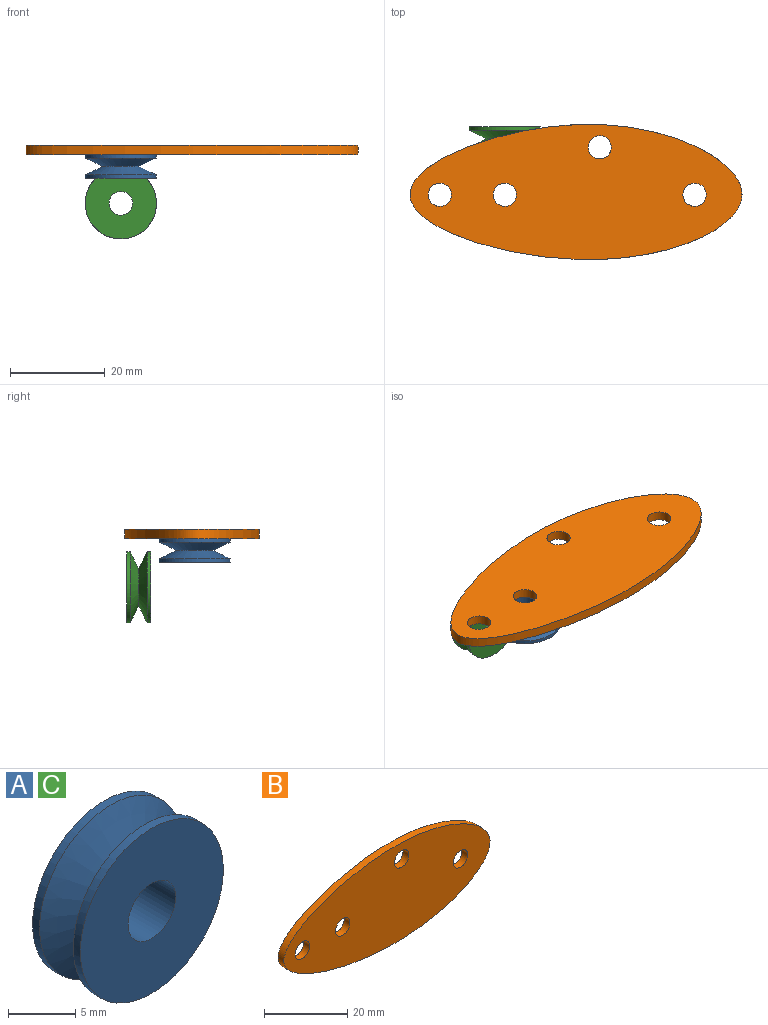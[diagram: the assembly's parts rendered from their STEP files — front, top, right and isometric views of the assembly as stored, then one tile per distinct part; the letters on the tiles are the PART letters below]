
ASSEMBLY  parts=3 mates=1
PART A: 7 faces, bbox 15x5x15 mm
  f0: cylinder r=7.5mm len=15mm, axis (0,1,0), area 34.4mm2, adj f3,f5
  f1: cylinder r=2.5mm len=5mm, axis (0,1,0), area 78.5mm2, adj f3,f4
  f2: cylinder r=7.5mm len=15mm, axis (0,1,0), area 34.4mm2, adj f4,f6
  f3: plane 15x15mm, normal (0,-1,0), area 157.1mm2, adj f0,f1
  f4: plane 15x15mm, normal (0,1,0), area 157.1mm2, adj f1,f2
  f5: cone r=7.56mm half-angle=64.3deg, axis (0,-1,0), area 145.2mm2, adj f0,f6
  f6: cone r=7.56mm half-angle=64.3deg, axis (0,1,0), area 145.2mm2, adj f2,f5
PART B: 7 faces, bbox 74.4x2x32.9 mm
  f0: extruded ~70x28.51mm, area 320.6mm2, adj f1,f2
  f1: plane 74.4x32.85mm, normal (0,-1,0), area 1448.4mm2, adj f0,f3,f4,f5,f6
  f2: plane 74.4x32.85mm, normal (0,1,0), area 1448.4mm2, adj f0,f3,f4,f5,f6
  f3: cylinder r=2.45mm len=4.9mm, axis (0,1,0), area 30.8mm2, adj f1,f2
  f4: cylinder r=2.45mm len=4.9mm, axis (0,1,0), area 30.8mm2, adj f1,f2
  f5: cylinder r=2.45mm len=4.9mm, axis (0,1,0), area 30.8mm2, adj f1,f2
  f6: cylinder r=2.45mm len=4.9mm, axis (0,1,0), area 30.8mm2, adj f1,f2
PART C: same geometry as A
PLACE A rot(axis=(-1,0,0),90deg) t=(0,-14.33,5.28)mm
PLACE B rot(axis=(-1,0,0),90deg) t=(0,-14.33,10.28)mm
PLACE C at identity
MATE fastened A.f0 <-> B.f3  axis (0,0,-1) through (-20,-14.33,10.28)mm
